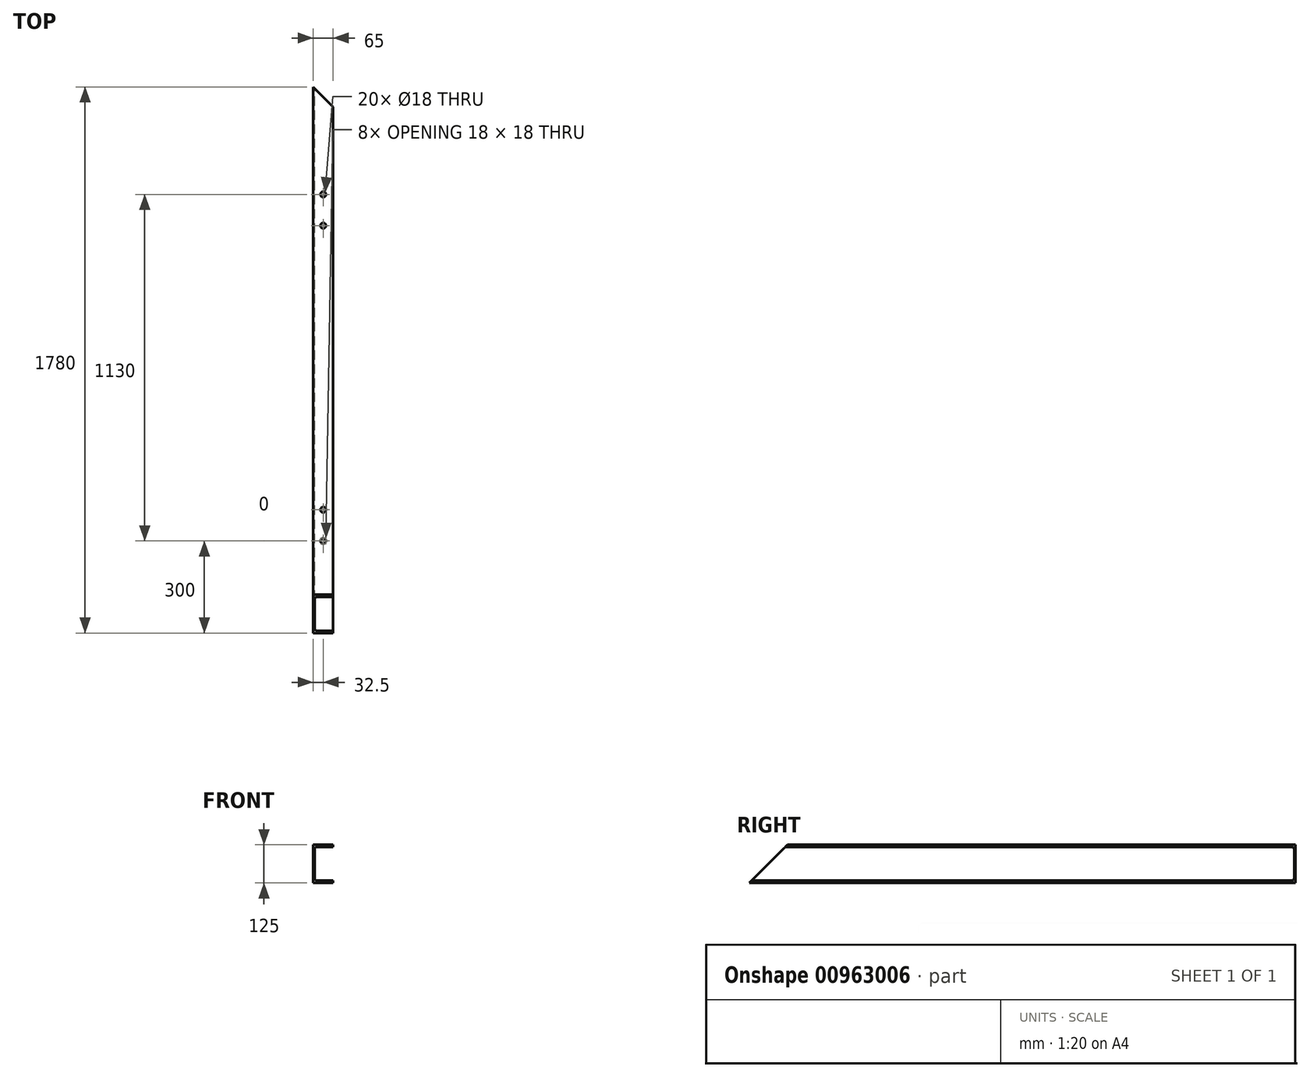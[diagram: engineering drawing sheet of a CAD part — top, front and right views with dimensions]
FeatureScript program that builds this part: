
annotation { "Feature Type Name" : "Feature", "Feature Type Description" : "" }
export const myFeature = defineFeature(function(context is Context, id is Id, definition is map)
    precondition{}
    {
        {
            var Q0;
            Q0=qCreatedBy(makeId("Front.planeOp"),FACE);
            var sketch = newSketch(context, id + "F0", { "sketchPlane" : qUnion([Q0])});
            skLineSegment(sketch, "E0", {"start": v(0, 0) * mm, "end": v(0, 125) * mm});
            skLineSegment(sketch, "E1", {"start": v(0, 125) * mm, "end": v(65, 125) * mm});
            skLineSegment(sketch, "E2", {"start": v(65, 125) * mm, "end": v(65, 117.5) * mm});
            skLineSegment(sketch, "E3", {"start": v(65, 117.5) * mm, "end": v(12.7, 117.5) * mm});
            skLineSegment(sketch, "E4", {"start": v(0, 0) * mm, "end": v(65, 0) * mm});
            skLineSegment(sketch, "E5", {"start": v(65, 0) * mm, "end": v(65, 7.5) * mm});
            skLineSegment(sketch, "E6", {"start": v(65, 7.5) * mm, "end": v(12.7, 7.5) * mm});
            skLineSegment(sketch, "E7", {"start": v(4.7, 15.5) * mm, "end": v(4.7, 109.5) * mm});
            skPoint(sketch, "E8.visualSharp", {"position": v(4.7, 117.5) * mm});
            skArc(sketch, "E8.filletArc", {"start": v(12.7, 117.5) * mm, "mid": v(7.04, 115.16) * mm, "end": v(4.7, 109.5) * mm});
            skPoint(sketch, "E9.visualSharp", {"position": v(4.7, 7.5) * mm});
            skArc(sketch, "E9.filletArc", {"start": v(4.7, 15.5) * mm, "mid": v(7.04, 9.84) * mm, "end": v(12.7, 7.5) * mm});
            skSolve(sketch);
        }
        {
            var Q0;
            Q0=makeQuery(id+"F0.imprint","IMPRINT",FACE,{"disambiguationData":[TD([[makeQuery(id+"F0.imprint","IMPRINT",EDGE,{"derivedFrom":sQuery(id+"F0.wireOp",EDGE,"E0")}),-1.0]])]});
            extrude(context, id + "F1", {"entities" : qUnion([Q0]), "depth" : 1780 * mm, "offsetDistance" : 25 * mm});
        }
        {
            var Q0;
            Q0=makeQuery(id+"F1.opExtrude","SWEPT_FACE",FACE,{"disambiguationData":[OSD([sQuery(id+"F0.wireOp",EDGE,"E1")])]});
            var sketch = newSketch(context, id + "F2", { "sketchPlane" : qUnion([Q0])});
            skLineSegment(sketch, "E10", {"start": v(65, 0) * mm, "end": v(65, -65) * mm});
            skLineSegment(sketch, "E11", {"start": v(65, -65) * mm, "end": v(0, 0) * mm});
            skSolve(sketch);
        }
        {
            var Q0;
            Q0=makeQuery(id+"F2.imprint","IMPRINT",FACE,{"disambiguationData":[TD([[makeQuery(id+"F2.imprint","IMPRINT",EDGE,{"derivedFrom":sQuery(id+"F2.wireOp",EDGE,"E10")}),1.0]])]});
            extrude(context, id + "F3", {"entities" : qUnion([Q0]), "operationType" : NewBodyOperationType.REMOVE, "endBound" : BoundingType.THROUGH_ALL, "oppositeDirection" : true, "depth" : 25 * mm, "offsetDistance" : 25 * mm});
        }
        {
            var Q0;
            Q0=makeQuery(id+"F1.opExtrude","SWEPT_FACE",FACE,{"disambiguationData":[OSD([sQuery(id+"F0.wireOp",EDGE,"E0")])]});
            var sketch = newSketch(context, id + "F4", { "sketchPlane" : qUnion([Q0])});
            skLineSegment(sketch, "E12", {"start": v(1780, 125) * mm, "end": v(1655, 125) * mm});
            skLineSegment(sketch, "E13", {"start": v(1655, 125) * mm, "end": v(1780, 0) * mm});
            skSolve(sketch);
        }
        {
            var Q0;
            Q0=makeQuery(id+"F4.imprint","IMPRINT",FACE,{"disambiguationData":[TD([[makeQuery(id+"F4.imprint","IMPRINT",EDGE,{"derivedFrom":sQuery(id+"F4.wireOp",EDGE,"E12")}),1.0]])]});
            extrude(context, id + "F5", {"entities" : qUnion([Q0]), "operationType" : NewBodyOperationType.REMOVE, "endBound" : BoundingType.THROUGH_ALL, "oppositeDirection" : true, "depth" : 25 * mm, "offsetDistance" : 25 * mm});
        }
        {
            var Q0;
            Q0=makeQuery(id+"F1.opExtrude","SWEPT_FACE",FACE,{"disambiguationData":[OSD([sQuery(id+"F0.wireOp",EDGE,"E1")])]});
            var sketch = newSketch(context, id + "F6", { "sketchPlane" : qUnion([Q0])});
            skCircle(sketch, "E14", {"center": v(32.5, -350) * mm, "radius": 9 * mm});
            skCircle(sketch, "E15", {"center": v(32.5, -452) * mm, "radius": 9 * mm});
            skSolve(sketch);
        }
        {
            var Q0;
            Q0=qSketchRegion(id+"F6",true);
            extrude(context, id + "F7", {"entities" : qUnion([Q0]), "operationType" : NewBodyOperationType.REMOVE, "endBound" : BoundingType.UP_TO_NEXT, "oppositeDirection" : true, "depth" : 25 * mm, "offsetDistance" : 25 * mm});
        }
        {
            var Q0;
            Q0=makeQuery(id+"F1.opExtrude","SWEPT_FACE",FACE,{"disambiguationData":[OSD([sQuery(id+"F0.wireOp",EDGE,"E1")])]});
            var sketch = newSketch(context, id + "F8", { "sketchPlane" : qUnion([Q0])});
            skCircle(sketch, "E16", {"center": v(32.5, -1378) * mm, "radius": 9 * mm});
            skCircle(sketch, "E17", {"center": v(32.5, -1480) * mm, "radius": 9 * mm});
            skLineSegment(sketch, "E18", {"start": v(32.5, -1655) * mm, "end": v(32.5, -1480) * mm, "construction": true});
            skLineSegment(sketch, "E19", {"start": v(32.5, -1480) * mm, "end": v(32.5, -1378) * mm, "construction": true});
            skSolve(sketch);
        }
        {
            var Q0;
            Q0=qSketchRegion(id+"F8",true);
            extrude(context, id + "F9", {"entities" : qUnion([Q0]), "operationType" : NewBodyOperationType.REMOVE, "endBound" : BoundingType.UP_TO_NEXT, "oppositeDirection" : true, "depth" : 25 * mm, "offsetDistance" : 25 * mm});
        }
    });
